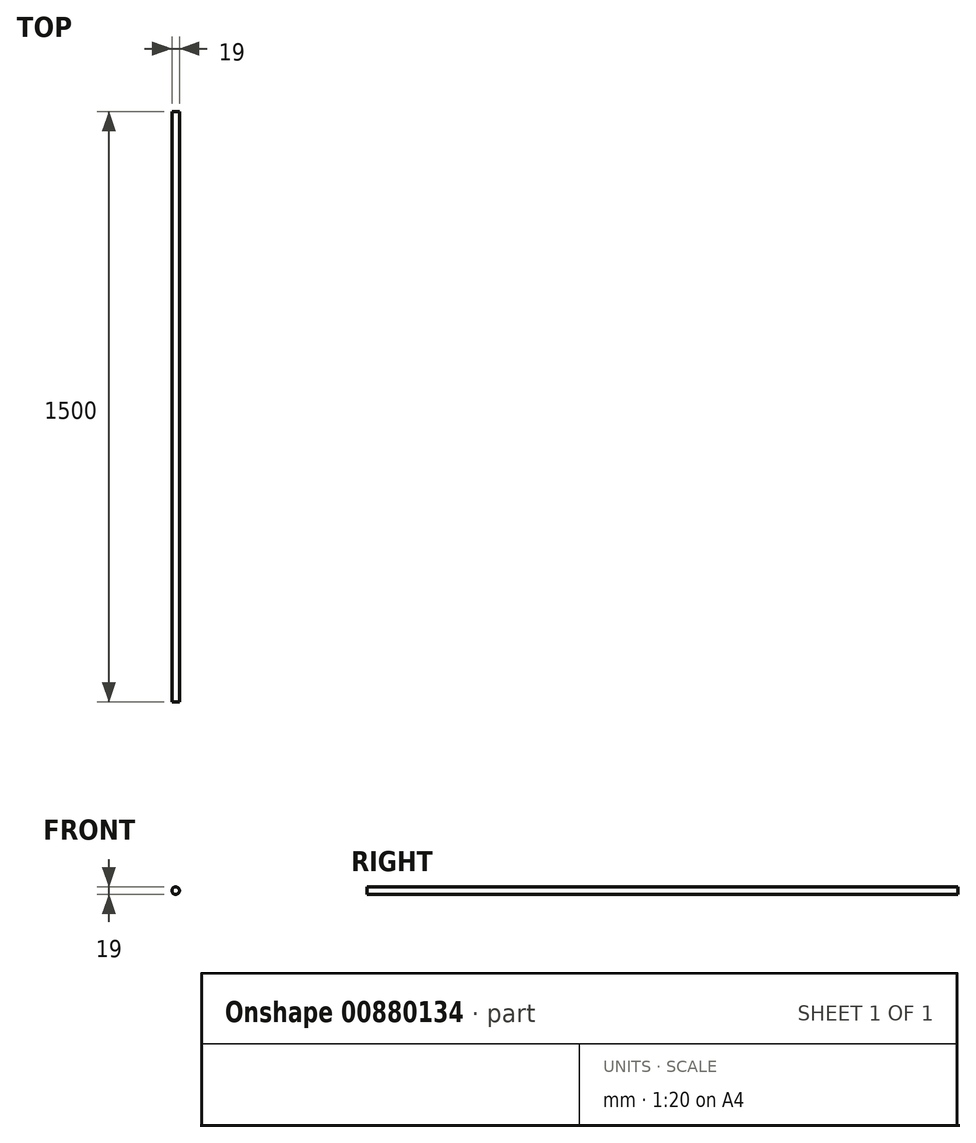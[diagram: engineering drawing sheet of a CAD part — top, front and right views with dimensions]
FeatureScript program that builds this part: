
annotation { "Feature Type Name" : "Feature", "Feature Type Description" : "" }
export const myFeature = defineFeature(function(context is Context, id is Id, definition is map)
    precondition{}
    {
        {
            var Q0;
            Q0=qCreatedBy(makeId("Front.planeOp"),FACE);
            var sketch = newSketch(context, id + "F0", { "sketchPlane" : qUnion([Q0])});
            skCircle(sketch, "E0", {"center": v(0, 0) * mm, "radius": 9.5 * mm});
            skSolve(sketch);
        }
        {
            var Q0;
            Q0 = qSketchRegion(id + "F0", true);
            extrude(context, id + "F1", {"entities" : qUnion([Q0]), "depth" : 1500 * mm, "offsetDistance" : 25 * mm});
        }
    });
